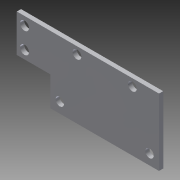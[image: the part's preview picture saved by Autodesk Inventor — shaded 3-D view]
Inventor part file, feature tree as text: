
AUTODESK INVENTOR PART (.ipt)
format: ipt  version: 2013 (Build 170138000, 138)  size: 128,512 bytes
history: native  units: in
note: dims shown in document units (in); Inventor stores cm internally (conversion verified against a paired STEP export)
features: sketch x4, reference x4, other x3, extrude x2, sheet_metal_op x1
ambient origin geometry x8: Origin, YZ Plane, XZ Plane, XY Plane, X Axis, Y Axis, Z Axis, Center Point
feature tree (14):
  sheet_metal_op  "Face2"
  sketch  "Sketch7"  dims[d3=0.295in d4=0.25in]
  extrude  "Extrusion3"  Depth=2.0in
  extrude  "Extrusion4"  Depth=0.25in
  other  "Plate5"
  sketch  "Sketch6"  dims[d1=2.244in d2=2.0in]
  reference  "Reference1"
  reference  "Reference2"
  sketch  "Sketch8"  dims[d5=0.295in]
  reference  "Reference3"
  reference  "Reference4"
  sketch  "Sketch12"  dims[d8=0.125in d19=0.25in d48=0.5in d51=2.0in d56=0.125in d57=0.5in d60=0.125in d61=0.0in d62=0.125in d63=0.0in d67=1.5in d70=1.0in d71=0.0in d72=1.0in d73=1.0in d74=0.0in]
  other  "Cut1"
  other  "Cut2"
